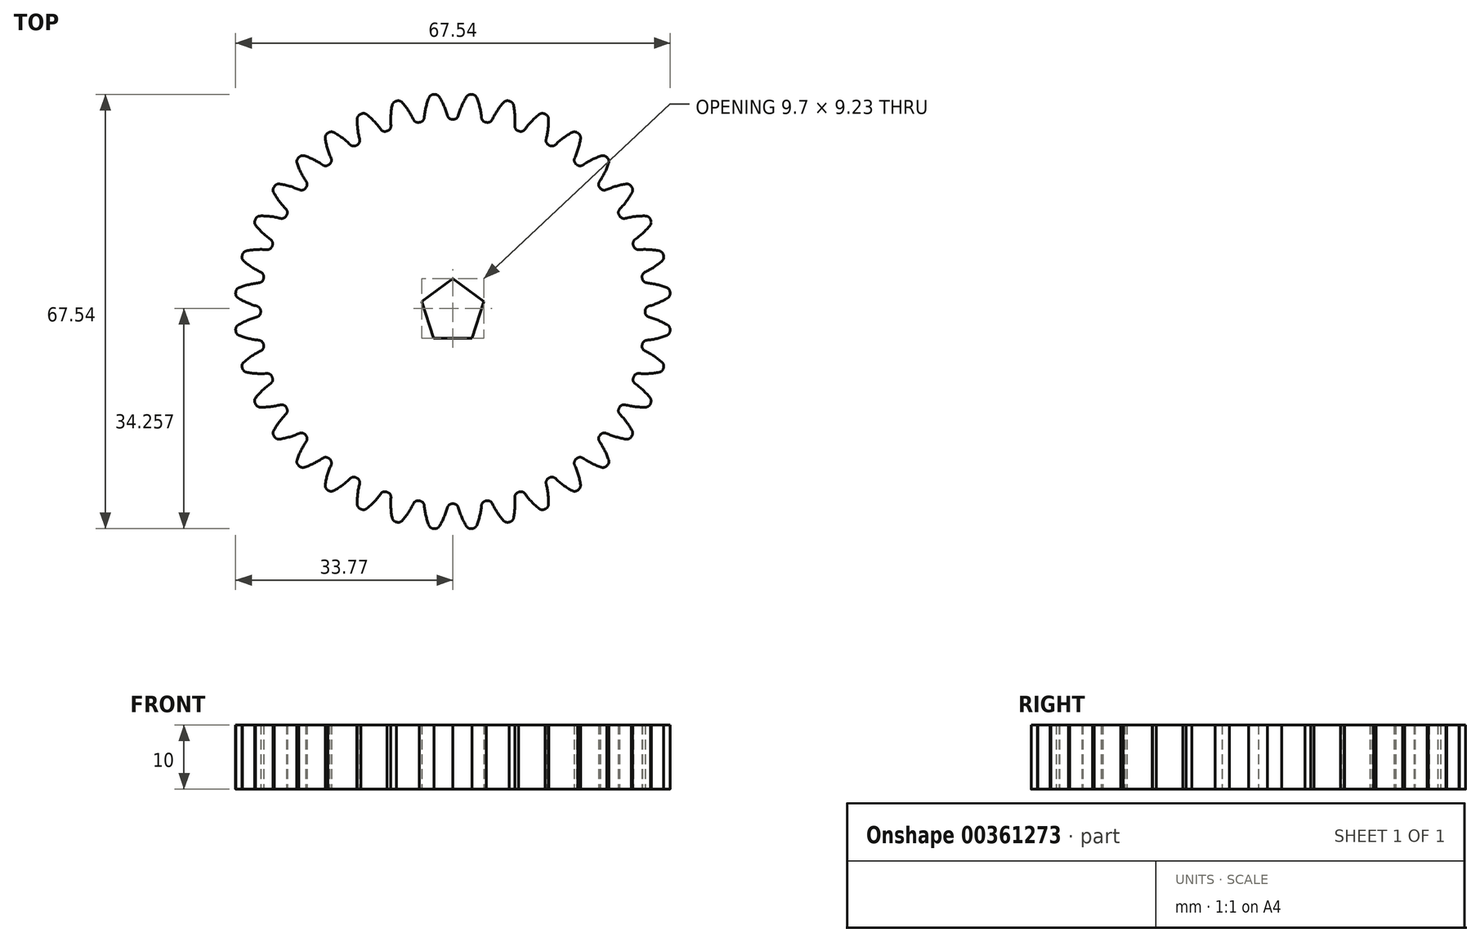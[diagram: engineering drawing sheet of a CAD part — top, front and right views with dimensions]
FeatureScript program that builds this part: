
annotation { "Feature Type Name" : "Feature", "Feature Type Description" : "" }
export const myFeature = defineFeature(function(context is Context, id is Id, definition is map)
    precondition{}
    {
        {
            var Q0;
            Q0=qCreatedBy(makeId("Top.planeOp"),FACE);
            var sketch = newSketch(context, id + "F0", { "sketchPlane" : qUnion([Q0])});
            skCircle(sketch, "E0", {"center": v(0, 0) * mm, "radius": 32.1 * mm, "construction": true});
            skCircle(sketch, "E1", {"center": v(0, 0) * mm, "radius": 33.88 * mm, "construction": true});
            skCircle(sketch, "E2", {"center": v(0, 0) * mm, "radius": 29.88 * mm, "construction": true});
            skLineSegment(sketch, "E3", {"start": v(0, 0) * mm, "end": v(0, 35.03) * mm, "construction": true});
            skLineSegment(sketch, "E4", {"start": v(0, 0) * mm, "end": v(-6.12, 34.73) * mm, "construction": true});
            skLineSegment(sketch, "E5", {"start": v(0, 0) * mm, "end": v(-3.06, 35) * mm, "construction": true});
            skCircle(sketch, "E6", {"center": v(-2.8, 31.98) * mm, "radius": 1.4 * mm, "construction": true});
            skCircle(sketch, "E7", {"center": v(-2.8, 31.98) * mm, "radius": 10 * mm, "construction": true});
            skArc(sketch, "E8", {"start": v(-1.92, 21.9) * mm, "mid": v(-1.88, 21.97) * mm, "end": v(-1.85, 22.02) * mm});
            skArc(sketch, "E9.trimOffspring", {"start": v(-0.85, 30.47) * mm, "mid": v(-1.38, 31.97) * mm, "end": v(-2.11, 33.38) * mm});
            skLineSegment(sketch, "E10", {"start": v(-2.85, 33.76) * mm, "end": v(-2.95, 33.76) * mm});
            skLineSegment(sketch, "E11", {"start": v(-0.07, 29.88) * mm, "end": v(0, 29.88) * mm});
            skPoint(sketch, "E12.visualSharp", {"position": v(-0.7, 29.87) * mm});
            skArc(sketch, "E12.filletArc", {"start": v(-0.85, 30.47) * mm, "mid": v(-0.56, 30.04) * mm, "end": v(-0.07, 29.88) * mm});
            skPoint(sketch, "E13.visualSharp", {"position": v(-2.38, 33.8) * mm});
            skArc(sketch, "E13.filletArc", {"start": v(-2.11, 33.38) * mm, "mid": v(-2.43, 33.68) * mm, "end": v(-2.85, 33.76) * mm});
            skArc(sketch, "E14.MirrorCS", {"start": v(-4.46, 30.15) * mm, "mid": v(-4.67, 29.68) * mm, "end": v(-5.12, 29.44) * mm});
            skLineSegment(sketch, "E15.MirrorCS", {"start": v(-5.12, 29.44) * mm, "end": v(-5.19, 29.43) * mm});
            skArc(sketch, "E16.MirrorCS", {"start": v(-4.46, 30.15) * mm, "mid": v(-4.2, 31.72) * mm, "end": v(-3.72, 33.24) * mm});
            skArc(sketch, "E17.MirrorCS", {"start": v(-3.72, 33.24) * mm, "mid": v(-3.46, 33.59) * mm, "end": v(-3.06, 33.75) * mm});
            skLineSegment(sketch, "E18.MirrorCS", {"start": v(-3.06, 33.75) * mm, "end": v(-2.95, 33.76) * mm});
            skArc(sketch, "E19.1.0", {"start": v(-6.12, 29.86) * mm, "mid": v(-5.76, 29.49) * mm, "end": v(-5.25, 29.41) * mm});
            skLineSegment(sketch, "E19.1.1", {"start": v(-5.25, 29.41) * mm, "end": v(-5.19, 29.43) * mm});
            skArc(sketch, "E19.1.2", {"start": v(-6.12, 29.86) * mm, "mid": v(-6.9, 31.25) * mm, "end": v(-7.88, 32.51) * mm});
            skArc(sketch, "E19.1.3", {"start": v(-7.88, 32.51) * mm, "mid": v(-8.24, 32.74) * mm, "end": v(-8.67, 32.76) * mm});
            skLineSegment(sketch, "E19.1.4", {"start": v(-8.67, 32.76) * mm, "end": v(-8.77, 32.73) * mm});
            skLineSegment(sketch, "E19.1.5", {"start": v(-8.87, 32.7) * mm, "end": v(-8.77, 32.73) * mm});
            skArc(sketch, "E19.1.6", {"start": v(-9.43, 32.1) * mm, "mid": v(-9.24, 32.48) * mm, "end": v(-8.87, 32.7) * mm});
            skArc(sketch, "E19.1.7", {"start": v(-9.63, 28.92) * mm, "mid": v(-9.64, 30.51) * mm, "end": v(-9.43, 32.1) * mm});
            skArc(sketch, "E19.1.8", {"start": v(-9.63, 28.92) * mm, "mid": v(-9.75, 28.42) * mm, "end": v(-10.16, 28.1) * mm});
            skLineSegment(sketch, "E19.1.9", {"start": v(-10.16, 28.1) * mm, "end": v(-10.22, 28.08) * mm});
            skArc(sketch, "E19.2.0", {"start": v(-11.22, 28.34) * mm, "mid": v(-10.8, 28.04) * mm, "end": v(-10.28, 28.05) * mm});
            skLineSegment(sketch, "E19.2.1", {"start": v(-10.28, 28.05) * mm, "end": v(-10.22, 28.08) * mm});
            skArc(sketch, "E19.2.2", {"start": v(-11.22, 28.34) * mm, "mid": v(-12.23, 29.57) * mm, "end": v(-13.4, 30.65) * mm});
            skArc(sketch, "E19.2.3", {"start": v(-13.4, 30.65) * mm, "mid": v(-13.8, 30.82) * mm, "end": v(-14.22, 30.75) * mm});
            skLineSegment(sketch, "E19.2.4", {"start": v(-14.22, 30.75) * mm, "end": v(-14.32, 30.71) * mm});
            skLineSegment(sketch, "E19.2.5", {"start": v(-14.41, 30.66) * mm, "end": v(-14.32, 30.71) * mm});
            skArc(sketch, "E19.2.6", {"start": v(-14.86, 29.97) * mm, "mid": v(-14.74, 30.38) * mm, "end": v(-14.41, 30.66) * mm});
            skArc(sketch, "E19.2.7", {"start": v(-14.5, 26.8) * mm, "mid": v(-14.8, 28.37) * mm, "end": v(-14.86, 29.97) * mm});
            skArc(sketch, "E19.2.8", {"start": v(-14.5, 26.8) * mm, "mid": v(-14.54, 26.3) * mm, "end": v(-14.88, 25.9) * mm});
            skLineSegment(sketch, "E19.2.9", {"start": v(-14.88, 25.9) * mm, "end": v(-14.94, 25.88) * mm});
            skArc(sketch, "E19.3.0", {"start": v(-15.97, 25.96) * mm, "mid": v(-15.5, 25.74) * mm, "end": v(-15, 25.84) * mm});
            skLineSegment(sketch, "E19.3.1", {"start": v(-15, 25.84) * mm, "end": v(-14.94, 25.88) * mm});
            skArc(sketch, "E19.3.2", {"start": v(-15.97, 25.96) * mm, "mid": v(-17.18, 27) * mm, "end": v(-18.52, 27.86) * mm});
            skArc(sketch, "E19.3.3", {"start": v(-18.52, 27.86) * mm, "mid": v(-18.94, 27.95) * mm, "end": v(-19.35, 27.82) * mm});
            skLineSegment(sketch, "E19.3.4", {"start": v(-19.35, 27.82) * mm, "end": v(-19.44, 27.76) * mm});
            skLineSegment(sketch, "E19.3.5", {"start": v(-19.52, 27.7) * mm, "end": v(-19.44, 27.76) * mm});
            skArc(sketch, "E19.3.6", {"start": v(-19.84, 26.93) * mm, "mid": v(-19.79, 27.36) * mm, "end": v(-19.52, 27.7) * mm});
            skArc(sketch, "E19.3.7", {"start": v(-18.94, 23.88) * mm, "mid": v(-19.5, 25.37) * mm, "end": v(-19.84, 26.93) * mm});
            skArc(sketch, "E19.3.8", {"start": v(-18.94, 23.88) * mm, "mid": v(-18.88, 23.37) * mm, "end": v(-19.16, 22.93) * mm});
            skLineSegment(sketch, "E19.3.9", {"start": v(-19.16, 22.93) * mm, "end": v(-19.2, 22.89) * mm});
            skArc(sketch, "E19.4.0", {"start": v(-20.23, 22.8) * mm, "mid": v(-19.74, 22.65) * mm, "end": v(-19.26, 22.85) * mm});
            skLineSegment(sketch, "E19.4.1", {"start": v(-19.26, 22.85) * mm, "end": v(-19.2, 22.89) * mm});
            skArc(sketch, "E19.4.2", {"start": v(-20.23, 22.8) * mm, "mid": v(-21.6, 23.6) * mm, "end": v(-23.08, 24.22) * mm});
            skArc(sketch, "E19.4.3", {"start": v(-23.08, 24.22) * mm, "mid": v(-23.5, 24.24) * mm, "end": v(-23.88, 24.03) * mm});
            skLineSegment(sketch, "E19.4.4", {"start": v(-23.88, 24.03) * mm, "end": v(-23.96, 23.96) * mm});
            skLineSegment(sketch, "E19.4.5", {"start": v(-24.03, 23.88) * mm, "end": v(-23.96, 23.96) * mm});
            skArc(sketch, "E19.4.6", {"start": v(-24.22, 23.08) * mm, "mid": v(-24.24, 23.5) * mm, "end": v(-24.03, 23.88) * mm});
            skArc(sketch, "E19.4.7", {"start": v(-22.8, 20.23) * mm, "mid": v(-23.6, 21.6) * mm, "end": v(-24.22, 23.08) * mm});
            skArc(sketch, "E19.4.8", {"start": v(-22.8, 20.23) * mm, "mid": v(-22.65, 19.74) * mm, "end": v(-22.85, 19.26) * mm});
            skLineSegment(sketch, "E19.4.9", {"start": v(-22.85, 19.26) * mm, "end": v(-22.89, 19.2) * mm});
            skArc(sketch, "E19.5.0", {"start": v(-23.88, 18.94) * mm, "mid": v(-23.37, 18.88) * mm, "end": v(-22.93, 19.16) * mm});
            skLineSegment(sketch, "E19.5.1", {"start": v(-22.93, 19.16) * mm, "end": v(-22.89, 19.2) * mm});
            skArc(sketch, "E19.5.2", {"start": v(-23.88, 18.94) * mm, "mid": v(-25.37, 19.5) * mm, "end": v(-26.93, 19.84) * mm});
            skArc(sketch, "E19.5.3", {"start": v(-26.93, 19.84) * mm, "mid": v(-27.36, 19.79) * mm, "end": v(-27.7, 19.52) * mm});
            skLineSegment(sketch, "E19.5.4", {"start": v(-27.7, 19.52) * mm, "end": v(-27.76, 19.44) * mm});
            skLineSegment(sketch, "E19.5.5", {"start": v(-27.82, 19.35) * mm, "end": v(-27.76, 19.44) * mm});
            skArc(sketch, "E19.5.6", {"start": v(-27.86, 18.52) * mm, "mid": v(-27.95, 18.94) * mm, "end": v(-27.82, 19.35) * mm});
            skArc(sketch, "E19.5.7", {"start": v(-25.96, 15.97) * mm, "mid": v(-27, 17.18) * mm, "end": v(-27.86, 18.52) * mm});
            skArc(sketch, "E19.5.8", {"start": v(-25.96, 15.97) * mm, "mid": v(-25.74, 15.5) * mm, "end": v(-25.84, 15) * mm});
            skLineSegment(sketch, "E19.5.9", {"start": v(-25.84, 15) * mm, "end": v(-25.88, 14.94) * mm});
            skArc(sketch, "E19.6.0", {"start": v(-26.8, 14.5) * mm, "mid": v(-26.3, 14.54) * mm, "end": v(-25.9, 14.88) * mm});
            skLineSegment(sketch, "E19.6.1", {"start": v(-25.9, 14.88) * mm, "end": v(-25.88, 14.94) * mm});
            skArc(sketch, "E19.6.2", {"start": v(-26.8, 14.5) * mm, "mid": v(-28.37, 14.8) * mm, "end": v(-29.97, 14.86) * mm});
            skArc(sketch, "E19.6.3", {"start": v(-29.97, 14.86) * mm, "mid": v(-30.38, 14.74) * mm, "end": v(-30.66, 14.41) * mm});
            skLineSegment(sketch, "E19.6.4", {"start": v(-30.66, 14.41) * mm, "end": v(-30.71, 14.32) * mm});
            skLineSegment(sketch, "E19.6.5", {"start": v(-30.75, 14.22) * mm, "end": v(-30.71, 14.32) * mm});
            skArc(sketch, "E19.6.6", {"start": v(-30.65, 13.4) * mm, "mid": v(-30.82, 13.8) * mm, "end": v(-30.75, 14.22) * mm});
            skArc(sketch, "E19.6.7", {"start": v(-28.34, 11.22) * mm, "mid": v(-29.57, 12.23) * mm, "end": v(-30.65, 13.4) * mm});
            skArc(sketch, "E19.6.8", {"start": v(-28.34, 11.22) * mm, "mid": v(-28.04, 10.8) * mm, "end": v(-28.05, 10.28) * mm});
            skLineSegment(sketch, "E19.6.9", {"start": v(-28.05, 10.28) * mm, "end": v(-28.08, 10.22) * mm});
            skArc(sketch, "E19.7.0", {"start": v(-28.92, 9.63) * mm, "mid": v(-28.42, 9.75) * mm, "end": v(-28.1, 10.16) * mm});
            skLineSegment(sketch, "E19.7.1", {"start": v(-28.1, 10.16) * mm, "end": v(-28.08, 10.22) * mm});
            skArc(sketch, "E19.7.2", {"start": v(-28.92, 9.63) * mm, "mid": v(-30.51, 9.64) * mm, "end": v(-32.1, 9.43) * mm});
            skArc(sketch, "E19.7.3", {"start": v(-32.1, 9.43) * mm, "mid": v(-32.48, 9.24) * mm, "end": v(-32.7, 8.87) * mm});
            skLineSegment(sketch, "E19.7.4", {"start": v(-32.7, 8.87) * mm, "end": v(-32.73, 8.77) * mm});
            skLineSegment(sketch, "E19.7.5", {"start": v(-32.76, 8.67) * mm, "end": v(-32.73, 8.77) * mm});
            skArc(sketch, "E19.7.6", {"start": v(-32.51, 7.88) * mm, "mid": v(-32.74, 8.24) * mm, "end": v(-32.76, 8.67) * mm});
            skArc(sketch, "E19.7.7", {"start": v(-29.86, 6.12) * mm, "mid": v(-31.25, 6.9) * mm, "end": v(-32.51, 7.88) * mm});
            skArc(sketch, "E19.7.8", {"start": v(-29.86, 6.12) * mm, "mid": v(-29.49, 5.76) * mm, "end": v(-29.41, 5.25) * mm});
            skLineSegment(sketch, "E19.7.9", {"start": v(-29.41, 5.25) * mm, "end": v(-29.43, 5.19) * mm});
            skArc(sketch, "E19.8.0", {"start": v(-30.15, 4.46) * mm, "mid": v(-29.68, 4.67) * mm, "end": v(-29.44, 5.12) * mm});
            skLineSegment(sketch, "E19.8.1", {"start": v(-29.44, 5.12) * mm, "end": v(-29.43, 5.19) * mm});
            skArc(sketch, "E19.8.2", {"start": v(-30.15, 4.46) * mm, "mid": v(-31.72, 4.2) * mm, "end": v(-33.24, 3.72) * mm});
            skArc(sketch, "E19.8.3", {"start": v(-33.24, 3.72) * mm, "mid": v(-33.59, 3.46) * mm, "end": v(-33.75, 3.06) * mm});
            skLineSegment(sketch, "E19.8.4", {"start": v(-33.75, 3.06) * mm, "end": v(-33.76, 2.95) * mm});
            skLineSegment(sketch, "E19.8.5", {"start": v(-33.76, 2.85) * mm, "end": v(-33.76, 2.95) * mm});
            skArc(sketch, "E19.8.6", {"start": v(-33.38, 2.11) * mm, "mid": v(-33.68, 2.43) * mm, "end": v(-33.76, 2.85) * mm});
            skArc(sketch, "E19.8.7", {"start": v(-30.47, 0.85) * mm, "mid": v(-31.97, 1.38) * mm, "end": v(-33.38, 2.11) * mm});
            skArc(sketch, "E19.8.8", {"start": v(-30.47, 0.85) * mm, "mid": v(-30.04, 0.56) * mm, "end": v(-29.88, 0.07) * mm});
            skLineSegment(sketch, "E19.8.9", {"start": v(-29.88, 0.07) * mm, "end": v(-29.88, 0) * mm});
            skArc(sketch, "E19.9.0", {"start": v(-30.47, -0.85) * mm, "mid": v(-30.04, -0.56) * mm, "end": v(-29.88, -0.07) * mm});
            skLineSegment(sketch, "E19.9.1", {"start": v(-29.88, -0.07) * mm, "end": v(-29.88, 0) * mm});
            skArc(sketch, "E19.9.2", {"start": v(-30.47, -0.85) * mm, "mid": v(-31.97, -1.38) * mm, "end": v(-33.38, -2.11) * mm});
            skArc(sketch, "E19.9.3", {"start": v(-33.38, -2.11) * mm, "mid": v(-33.68, -2.43) * mm, "end": v(-33.76, -2.85) * mm});
            skLineSegment(sketch, "E19.9.4", {"start": v(-33.76, -2.85) * mm, "end": v(-33.76, -2.95) * mm});
            skLineSegment(sketch, "E19.9.5", {"start": v(-33.75, -3.06) * mm, "end": v(-33.76, -2.95) * mm});
            skArc(sketch, "E19.9.6", {"start": v(-33.24, -3.72) * mm, "mid": v(-33.59, -3.46) * mm, "end": v(-33.75, -3.06) * mm});
            skArc(sketch, "E19.9.7", {"start": v(-30.15, -4.46) * mm, "mid": v(-31.72, -4.2) * mm, "end": v(-33.24, -3.72) * mm});
            skArc(sketch, "E19.9.8", {"start": v(-30.15, -4.46) * mm, "mid": v(-29.68, -4.67) * mm, "end": v(-29.44, -5.12) * mm});
            skLineSegment(sketch, "E19.9.9", {"start": v(-29.44, -5.12) * mm, "end": v(-29.43, -5.19) * mm});
            skArc(sketch, "E19.10.0", {"start": v(-29.86, -6.12) * mm, "mid": v(-29.49, -5.76) * mm, "end": v(-29.41, -5.25) * mm});
            skLineSegment(sketch, "E19.10.1", {"start": v(-29.41, -5.25) * mm, "end": v(-29.43, -5.19) * mm});
            skArc(sketch, "E19.10.2", {"start": v(-29.86, -6.12) * mm, "mid": v(-31.25, -6.9) * mm, "end": v(-32.51, -7.88) * mm});
            skArc(sketch, "E19.10.3", {"start": v(-32.51, -7.88) * mm, "mid": v(-32.74, -8.24) * mm, "end": v(-32.76, -8.67) * mm});
            skLineSegment(sketch, "E19.10.4", {"start": v(-32.76, -8.67) * mm, "end": v(-32.73, -8.77) * mm});
            skLineSegment(sketch, "E19.10.5", {"start": v(-32.7, -8.87) * mm, "end": v(-32.73, -8.77) * mm});
            skArc(sketch, "E19.10.6", {"start": v(-32.1, -9.43) * mm, "mid": v(-32.48, -9.24) * mm, "end": v(-32.7, -8.87) * mm});
            skArc(sketch, "E19.10.7", {"start": v(-28.92, -9.63) * mm, "mid": v(-30.51, -9.64) * mm, "end": v(-32.1, -9.43) * mm});
            skArc(sketch, "E19.10.8", {"start": v(-28.92, -9.63) * mm, "mid": v(-28.42, -9.75) * mm, "end": v(-28.1, -10.16) * mm});
            skLineSegment(sketch, "E19.10.9", {"start": v(-28.1, -10.16) * mm, "end": v(-28.08, -10.22) * mm});
            skArc(sketch, "E19.11.0", {"start": v(-28.34, -11.22) * mm, "mid": v(-28.04, -10.8) * mm, "end": v(-28.05, -10.28) * mm});
            skLineSegment(sketch, "E19.11.1", {"start": v(-28.05, -10.28) * mm, "end": v(-28.08, -10.22) * mm});
            skArc(sketch, "E19.11.2", {"start": v(-28.34, -11.22) * mm, "mid": v(-29.57, -12.23) * mm, "end": v(-30.65, -13.4) * mm});
            skArc(sketch, "E19.11.3", {"start": v(-30.65, -13.4) * mm, "mid": v(-30.82, -13.8) * mm, "end": v(-30.75, -14.22) * mm});
            skLineSegment(sketch, "E19.11.4", {"start": v(-30.75, -14.22) * mm, "end": v(-30.71, -14.32) * mm});
            skLineSegment(sketch, "E19.11.5", {"start": v(-30.66, -14.41) * mm, "end": v(-30.71, -14.32) * mm});
            skArc(sketch, "E19.11.6", {"start": v(-29.97, -14.86) * mm, "mid": v(-30.38, -14.74) * mm, "end": v(-30.66, -14.41) * mm});
            skArc(sketch, "E19.11.7", {"start": v(-26.8, -14.5) * mm, "mid": v(-28.37, -14.8) * mm, "end": v(-29.97, -14.86) * mm});
            skArc(sketch, "E19.11.8", {"start": v(-26.8, -14.5) * mm, "mid": v(-26.3, -14.54) * mm, "end": v(-25.9, -14.88) * mm});
            skLineSegment(sketch, "E19.11.9", {"start": v(-25.9, -14.88) * mm, "end": v(-25.88, -14.94) * mm});
            skArc(sketch, "E19.12.0", {"start": v(-25.96, -15.97) * mm, "mid": v(-25.74, -15.5) * mm, "end": v(-25.84, -15) * mm});
            skLineSegment(sketch, "E19.12.1", {"start": v(-25.84, -15) * mm, "end": v(-25.88, -14.94) * mm});
            skArc(sketch, "E19.12.2", {"start": v(-25.96, -15.97) * mm, "mid": v(-27, -17.18) * mm, "end": v(-27.86, -18.52) * mm});
            skArc(sketch, "E19.12.3", {"start": v(-27.86, -18.52) * mm, "mid": v(-27.95, -18.94) * mm, "end": v(-27.82, -19.35) * mm});
            skLineSegment(sketch, "E19.12.4", {"start": v(-27.82, -19.35) * mm, "end": v(-27.76, -19.44) * mm});
            skLineSegment(sketch, "E19.12.5", {"start": v(-27.7, -19.52) * mm, "end": v(-27.76, -19.44) * mm});
            skArc(sketch, "E19.12.6", {"start": v(-26.93, -19.84) * mm, "mid": v(-27.36, -19.79) * mm, "end": v(-27.7, -19.52) * mm});
            skArc(sketch, "E19.12.7", {"start": v(-23.88, -18.94) * mm, "mid": v(-25.37, -19.5) * mm, "end": v(-26.93, -19.84) * mm});
            skArc(sketch, "E19.12.8", {"start": v(-23.88, -18.94) * mm, "mid": v(-23.37, -18.88) * mm, "end": v(-22.93, -19.16) * mm});
            skLineSegment(sketch, "E19.12.9", {"start": v(-22.93, -19.16) * mm, "end": v(-22.89, -19.2) * mm});
            skArc(sketch, "E19.13.0", {"start": v(-22.8, -20.23) * mm, "mid": v(-22.65, -19.74) * mm, "end": v(-22.85, -19.26) * mm});
            skLineSegment(sketch, "E19.13.1", {"start": v(-22.85, -19.26) * mm, "end": v(-22.89, -19.2) * mm});
            skArc(sketch, "E19.13.2", {"start": v(-22.8, -20.23) * mm, "mid": v(-23.6, -21.6) * mm, "end": v(-24.22, -23.08) * mm});
            skArc(sketch, "E19.13.3", {"start": v(-24.22, -23.08) * mm, "mid": v(-24.24, -23.5) * mm, "end": v(-24.03, -23.88) * mm});
            skLineSegment(sketch, "E19.13.4", {"start": v(-24.03, -23.88) * mm, "end": v(-23.96, -23.96) * mm});
            skLineSegment(sketch, "E19.13.5", {"start": v(-23.88, -24.03) * mm, "end": v(-23.96, -23.96) * mm});
            skArc(sketch, "E19.13.6", {"start": v(-23.08, -24.22) * mm, "mid": v(-23.5, -24.24) * mm, "end": v(-23.88, -24.03) * mm});
            skArc(sketch, "E19.13.7", {"start": v(-20.23, -22.8) * mm, "mid": v(-21.6, -23.6) * mm, "end": v(-23.08, -24.22) * mm});
            skArc(sketch, "E19.13.8", {"start": v(-20.23, -22.8) * mm, "mid": v(-19.74, -22.65) * mm, "end": v(-19.26, -22.85) * mm});
            skLineSegment(sketch, "E19.13.9", {"start": v(-19.26, -22.85) * mm, "end": v(-19.2, -22.89) * mm});
            skArc(sketch, "E19.14.0", {"start": v(-18.94, -23.88) * mm, "mid": v(-18.88, -23.37) * mm, "end": v(-19.16, -22.93) * mm});
            skLineSegment(sketch, "E19.14.1", {"start": v(-19.16, -22.93) * mm, "end": v(-19.2, -22.89) * mm});
            skArc(sketch, "E19.14.2", {"start": v(-18.94, -23.88) * mm, "mid": v(-19.5, -25.37) * mm, "end": v(-19.84, -26.93) * mm});
            skArc(sketch, "E19.14.3", {"start": v(-19.84, -26.93) * mm, "mid": v(-19.79, -27.36) * mm, "end": v(-19.52, -27.7) * mm});
            skLineSegment(sketch, "E19.14.4", {"start": v(-19.52, -27.7) * mm, "end": v(-19.44, -27.76) * mm});
            skLineSegment(sketch, "E19.14.5", {"start": v(-19.35, -27.82) * mm, "end": v(-19.44, -27.76) * mm});
            skArc(sketch, "E19.14.6", {"start": v(-18.52, -27.86) * mm, "mid": v(-18.94, -27.95) * mm, "end": v(-19.35, -27.82) * mm});
            skArc(sketch, "E19.14.7", {"start": v(-15.97, -25.96) * mm, "mid": v(-17.18, -27) * mm, "end": v(-18.52, -27.86) * mm});
            skArc(sketch, "E19.14.8", {"start": v(-15.97, -25.96) * mm, "mid": v(-15.5, -25.74) * mm, "end": v(-15, -25.84) * mm});
            skLineSegment(sketch, "E19.14.9", {"start": v(-15, -25.84) * mm, "end": v(-14.94, -25.88) * mm});
            skArc(sketch, "E19.15.0", {"start": v(-14.5, -26.8) * mm, "mid": v(-14.54, -26.3) * mm, "end": v(-14.88, -25.9) * mm});
            skLineSegment(sketch, "E19.15.1", {"start": v(-14.88, -25.9) * mm, "end": v(-14.94, -25.88) * mm});
            skArc(sketch, "E19.15.2", {"start": v(-14.5, -26.8) * mm, "mid": v(-14.8, -28.37) * mm, "end": v(-14.86, -29.97) * mm});
            skArc(sketch, "E19.15.3", {"start": v(-14.86, -29.97) * mm, "mid": v(-14.74, -30.38) * mm, "end": v(-14.41, -30.66) * mm});
            skLineSegment(sketch, "E19.15.4", {"start": v(-14.41, -30.66) * mm, "end": v(-14.32, -30.71) * mm});
            skLineSegment(sketch, "E19.15.5", {"start": v(-14.22, -30.75) * mm, "end": v(-14.32, -30.71) * mm});
            skArc(sketch, "E19.15.6", {"start": v(-13.4, -30.65) * mm, "mid": v(-13.8, -30.82) * mm, "end": v(-14.22, -30.75) * mm});
            skArc(sketch, "E19.15.7", {"start": v(-11.22, -28.34) * mm, "mid": v(-12.23, -29.57) * mm, "end": v(-13.4, -30.65) * mm});
            skArc(sketch, "E19.15.8", {"start": v(-11.22, -28.34) * mm, "mid": v(-10.8, -28.04) * mm, "end": v(-10.28, -28.05) * mm});
            skLineSegment(sketch, "E19.15.9", {"start": v(-10.28, -28.05) * mm, "end": v(-10.22, -28.08) * mm});
            skArc(sketch, "E19.16.0", {"start": v(-9.63, -28.92) * mm, "mid": v(-9.75, -28.42) * mm, "end": v(-10.16, -28.1) * mm});
            skLineSegment(sketch, "E19.16.1", {"start": v(-10.16, -28.1) * mm, "end": v(-10.22, -28.08) * mm});
            skArc(sketch, "E19.16.2", {"start": v(-9.63, -28.92) * mm, "mid": v(-9.64, -30.51) * mm, "end": v(-9.43, -32.1) * mm});
            skArc(sketch, "E19.16.3", {"start": v(-9.43, -32.1) * mm, "mid": v(-9.24, -32.48) * mm, "end": v(-8.87, -32.7) * mm});
            skLineSegment(sketch, "E19.16.4", {"start": v(-8.87, -32.7) * mm, "end": v(-8.77, -32.73) * mm});
            skLineSegment(sketch, "E19.16.5", {"start": v(-8.67, -32.76) * mm, "end": v(-8.77, -32.73) * mm});
            skArc(sketch, "E19.16.6", {"start": v(-7.88, -32.5) * mm, "mid": v(-8.24, -32.74) * mm, "end": v(-8.67, -32.76) * mm});
            skArc(sketch, "E19.16.7", {"start": v(-6.12, -29.86) * mm, "mid": v(-6.9, -31.25) * mm, "end": v(-7.88, -32.5) * mm});
            skArc(sketch, "E19.16.8", {"start": v(-6.12, -29.86) * mm, "mid": v(-5.76, -29.49) * mm, "end": v(-5.25, -29.41) * mm});
            skLineSegment(sketch, "E19.16.9", {"start": v(-5.25, -29.41) * mm, "end": v(-5.19, -29.43) * mm});
            skArc(sketch, "E19.17.0", {"start": v(-4.46, -30.15) * mm, "mid": v(-4.67, -29.68) * mm, "end": v(-5.12, -29.44) * mm});
            skLineSegment(sketch, "E19.17.1", {"start": v(-5.12, -29.44) * mm, "end": v(-5.19, -29.43) * mm});
            skArc(sketch, "E19.17.2", {"start": v(-4.46, -30.15) * mm, "mid": v(-4.2, -31.72) * mm, "end": v(-3.72, -33.24) * mm});
            skArc(sketch, "E19.17.3", {"start": v(-3.72, -33.24) * mm, "mid": v(-3.46, -33.59) * mm, "end": v(-3.06, -33.74) * mm});
            skLineSegment(sketch, "E19.17.4", {"start": v(-3.06, -33.74) * mm, "end": v(-2.95, -33.76) * mm});
            skLineSegment(sketch, "E19.17.5", {"start": v(-2.85, -33.76) * mm, "end": v(-2.95, -33.76) * mm});
            skArc(sketch, "E19.17.6", {"start": v(-2.11, -33.38) * mm, "mid": v(-2.43, -33.68) * mm, "end": v(-2.85, -33.76) * mm});
            skArc(sketch, "E19.17.7", {"start": v(-0.85, -30.47) * mm, "mid": v(-1.38, -31.97) * mm, "end": v(-2.11, -33.38) * mm});
            skArc(sketch, "E19.17.8", {"start": v(-0.85, -30.47) * mm, "mid": v(-0.56, -30.04) * mm, "end": v(-0.07, -29.88) * mm});
            skLineSegment(sketch, "E19.17.9", {"start": v(-0.07, -29.88) * mm, "end": v(0, -29.88) * mm});
            skArc(sketch, "E19.18.0", {"start": v(0.85, -30.47) * mm, "mid": v(0.56, -30.04) * mm, "end": v(0.07, -29.88) * mm});
            skLineSegment(sketch, "E19.18.1", {"start": v(0.07, -29.88) * mm, "end": v(0, -29.88) * mm});
            skArc(sketch, "E19.18.2", {"start": v(0.85, -30.47) * mm, "mid": v(1.38, -31.97) * mm, "end": v(2.11, -33.38) * mm});
            skArc(sketch, "E19.18.3", {"start": v(2.11, -33.38) * mm, "mid": v(2.43, -33.68) * mm, "end": v(2.85, -33.76) * mm});
            skLineSegment(sketch, "E19.18.4", {"start": v(2.85, -33.76) * mm, "end": v(2.95, -33.76) * mm});
            skLineSegment(sketch, "E19.18.5", {"start": v(3.06, -33.74) * mm, "end": v(2.95, -33.76) * mm});
            skArc(sketch, "E19.18.6", {"start": v(3.72, -33.24) * mm, "mid": v(3.46, -33.59) * mm, "end": v(3.06, -33.74) * mm});
            skArc(sketch, "E19.18.7", {"start": v(4.46, -30.15) * mm, "mid": v(4.2, -31.72) * mm, "end": v(3.72, -33.24) * mm});
            skArc(sketch, "E19.18.8", {"start": v(4.46, -30.15) * mm, "mid": v(4.67, -29.68) * mm, "end": v(5.12, -29.44) * mm});
            skLineSegment(sketch, "E19.18.9", {"start": v(5.12, -29.44) * mm, "end": v(5.19, -29.43) * mm});
            skArc(sketch, "E19.19.0", {"start": v(6.12, -29.86) * mm, "mid": v(5.76, -29.49) * mm, "end": v(5.25, -29.41) * mm});
            skLineSegment(sketch, "E19.19.1", {"start": v(5.25, -29.41) * mm, "end": v(5.19, -29.43) * mm});
            skArc(sketch, "E19.19.2", {"start": v(6.12, -29.86) * mm, "mid": v(6.9, -31.25) * mm, "end": v(7.88, -32.5) * mm});
            skArc(sketch, "E19.19.3", {"start": v(7.88, -32.5) * mm, "mid": v(8.24, -32.74) * mm, "end": v(8.67, -32.76) * mm});
            skLineSegment(sketch, "E19.19.4", {"start": v(8.67, -32.76) * mm, "end": v(8.77, -32.73) * mm});
            skLineSegment(sketch, "E19.19.5", {"start": v(8.87, -32.7) * mm, "end": v(8.77, -32.73) * mm});
            skArc(sketch, "E19.19.6", {"start": v(9.43, -32.1) * mm, "mid": v(9.24, -32.48) * mm, "end": v(8.87, -32.7) * mm});
            skArc(sketch, "E19.19.7", {"start": v(9.63, -28.92) * mm, "mid": v(9.64, -30.51) * mm, "end": v(9.43, -32.1) * mm});
            skArc(sketch, "E19.19.8", {"start": v(9.63, -28.92) * mm, "mid": v(9.75, -28.42) * mm, "end": v(10.16, -28.1) * mm});
            skLineSegment(sketch, "E19.19.9", {"start": v(10.16, -28.1) * mm, "end": v(10.22, -28.08) * mm});
            skArc(sketch, "E19.20.0", {"start": v(11.22, -28.34) * mm, "mid": v(10.8, -28.04) * mm, "end": v(10.28, -28.05) * mm});
            skLineSegment(sketch, "E19.20.1", {"start": v(10.28, -28.05) * mm, "end": v(10.22, -28.08) * mm});
            skArc(sketch, "E19.20.2", {"start": v(11.22, -28.34) * mm, "mid": v(12.23, -29.57) * mm, "end": v(13.4, -30.65) * mm});
            skArc(sketch, "E19.20.3", {"start": v(13.4, -30.65) * mm, "mid": v(13.8, -30.82) * mm, "end": v(14.22, -30.75) * mm});
            skLineSegment(sketch, "E19.20.4", {"start": v(14.22, -30.75) * mm, "end": v(14.32, -30.71) * mm});
            skLineSegment(sketch, "E19.20.5", {"start": v(14.41, -30.66) * mm, "end": v(14.32, -30.71) * mm});
            skArc(sketch, "E19.20.6", {"start": v(14.86, -29.97) * mm, "mid": v(14.74, -30.38) * mm, "end": v(14.41, -30.66) * mm});
            skArc(sketch, "E19.20.7", {"start": v(14.5, -26.8) * mm, "mid": v(14.8, -28.37) * mm, "end": v(14.86, -29.97) * mm});
            skArc(sketch, "E19.20.8", {"start": v(14.5, -26.8) * mm, "mid": v(14.54, -26.3) * mm, "end": v(14.88, -25.9) * mm});
            skLineSegment(sketch, "E19.20.9", {"start": v(14.88, -25.9) * mm, "end": v(14.94, -25.88) * mm});
            skArc(sketch, "E19.21.0", {"start": v(15.97, -25.96) * mm, "mid": v(15.5, -25.74) * mm, "end": v(15, -25.84) * mm});
            skLineSegment(sketch, "E19.21.1", {"start": v(15, -25.84) * mm, "end": v(14.94, -25.88) * mm});
            skArc(sketch, "E19.21.2", {"start": v(15.97, -25.96) * mm, "mid": v(17.18, -27) * mm, "end": v(18.52, -27.86) * mm});
            skArc(sketch, "E19.21.3", {"start": v(18.52, -27.86) * mm, "mid": v(18.94, -27.95) * mm, "end": v(19.35, -27.82) * mm});
            skLineSegment(sketch, "E19.21.4", {"start": v(19.35, -27.82) * mm, "end": v(19.44, -27.76) * mm});
            skLineSegment(sketch, "E19.21.5", {"start": v(19.52, -27.7) * mm, "end": v(19.44, -27.76) * mm});
            skArc(sketch, "E19.21.6", {"start": v(19.84, -26.93) * mm, "mid": v(19.79, -27.36) * mm, "end": v(19.52, -27.7) * mm});
            skArc(sketch, "E19.21.7", {"start": v(18.94, -23.88) * mm, "mid": v(19.5, -25.37) * mm, "end": v(19.84, -26.93) * mm});
            skArc(sketch, "E19.21.8", {"start": v(18.94, -23.88) * mm, "mid": v(18.88, -23.37) * mm, "end": v(19.16, -22.93) * mm});
            skLineSegment(sketch, "E19.21.9", {"start": v(19.16, -22.93) * mm, "end": v(19.2, -22.89) * mm});
            skArc(sketch, "E19.22.0", {"start": v(20.23, -22.8) * mm, "mid": v(19.74, -22.65) * mm, "end": v(19.26, -22.85) * mm});
            skLineSegment(sketch, "E19.22.1", {"start": v(19.26, -22.85) * mm, "end": v(19.2, -22.89) * mm});
            skArc(sketch, "E19.22.2", {"start": v(20.23, -22.8) * mm, "mid": v(21.6, -23.6) * mm, "end": v(23.08, -24.22) * mm});
            skArc(sketch, "E19.22.3", {"start": v(23.08, -24.22) * mm, "mid": v(23.5, -24.24) * mm, "end": v(23.88, -24.03) * mm});
            skLineSegment(sketch, "E19.22.4", {"start": v(23.88, -24.03) * mm, "end": v(23.96, -23.96) * mm});
            skLineSegment(sketch, "E19.22.5", {"start": v(24.03, -23.88) * mm, "end": v(23.96, -23.96) * mm});
            skArc(sketch, "E19.22.6", {"start": v(24.22, -23.08) * mm, "mid": v(24.24, -23.5) * mm, "end": v(24.03, -23.88) * mm});
            skArc(sketch, "E19.22.7", {"start": v(22.8, -20.23) * mm, "mid": v(23.6, -21.6) * mm, "end": v(24.22, -23.08) * mm});
            skArc(sketch, "E19.22.8", {"start": v(22.8, -20.23) * mm, "mid": v(22.65, -19.74) * mm, "end": v(22.85, -19.26) * mm});
            skLineSegment(sketch, "E19.22.9", {"start": v(22.85, -19.26) * mm, "end": v(22.89, -19.2) * mm});
            skArc(sketch, "E19.23.0", {"start": v(23.88, -18.94) * mm, "mid": v(23.37, -18.88) * mm, "end": v(22.93, -19.16) * mm});
            skLineSegment(sketch, "E19.23.1", {"start": v(22.93, -19.16) * mm, "end": v(22.89, -19.2) * mm});
            skArc(sketch, "E19.23.2", {"start": v(23.88, -18.94) * mm, "mid": v(25.37, -19.5) * mm, "end": v(26.93, -19.84) * mm});
            skArc(sketch, "E19.23.3", {"start": v(26.93, -19.84) * mm, "mid": v(27.36, -19.79) * mm, "end": v(27.7, -19.52) * mm});
            skLineSegment(sketch, "E19.23.4", {"start": v(27.7, -19.52) * mm, "end": v(27.76, -19.44) * mm});
            skLineSegment(sketch, "E19.23.5", {"start": v(27.82, -19.35) * mm, "end": v(27.76, -19.44) * mm});
            skArc(sketch, "E19.23.6", {"start": v(27.86, -18.52) * mm, "mid": v(27.95, -18.94) * mm, "end": v(27.82, -19.35) * mm});
            skArc(sketch, "E19.23.7", {"start": v(25.96, -15.97) * mm, "mid": v(27, -17.18) * mm, "end": v(27.86, -18.52) * mm});
            skArc(sketch, "E19.23.8", {"start": v(25.96, -15.97) * mm, "mid": v(25.74, -15.5) * mm, "end": v(25.84, -15) * mm});
            skLineSegment(sketch, "E19.23.9", {"start": v(25.84, -15) * mm, "end": v(25.88, -14.94) * mm});
            skArc(sketch, "E19.24.0", {"start": v(26.8, -14.5) * mm, "mid": v(26.3, -14.54) * mm, "end": v(25.9, -14.88) * mm});
            skLineSegment(sketch, "E19.24.1", {"start": v(25.9, -14.88) * mm, "end": v(25.88, -14.94) * mm});
            skArc(sketch, "E19.24.2", {"start": v(26.8, -14.5) * mm, "mid": v(28.37, -14.8) * mm, "end": v(29.97, -14.86) * mm});
            skArc(sketch, "E19.24.3", {"start": v(29.97, -14.86) * mm, "mid": v(30.38, -14.74) * mm, "end": v(30.66, -14.41) * mm});
            skLineSegment(sketch, "E19.24.4", {"start": v(30.66, -14.41) * mm, "end": v(30.71, -14.32) * mm});
            skLineSegment(sketch, "E19.24.5", {"start": v(30.75, -14.22) * mm, "end": v(30.71, -14.32) * mm});
            skArc(sketch, "E19.24.6", {"start": v(30.65, -13.4) * mm, "mid": v(30.82, -13.8) * mm, "end": v(30.75, -14.22) * mm});
            skArc(sketch, "E19.24.7", {"start": v(28.34, -11.22) * mm, "mid": v(29.57, -12.23) * mm, "end": v(30.65, -13.4) * mm});
            skArc(sketch, "E19.24.8", {"start": v(28.34, -11.22) * mm, "mid": v(28.04, -10.8) * mm, "end": v(28.05, -10.28) * mm});
            skLineSegment(sketch, "E19.24.9", {"start": v(28.05, -10.28) * mm, "end": v(28.08, -10.22) * mm});
            skArc(sketch, "E19.25.0", {"start": v(28.92, -9.63) * mm, "mid": v(28.42, -9.75) * mm, "end": v(28.1, -10.16) * mm});
            skLineSegment(sketch, "E19.25.1", {"start": v(28.1, -10.16) * mm, "end": v(28.08, -10.22) * mm});
            skArc(sketch, "E19.25.2", {"start": v(28.92, -9.63) * mm, "mid": v(30.51, -9.64) * mm, "end": v(32.1, -9.43) * mm});
            skArc(sketch, "E19.25.3", {"start": v(32.1, -9.43) * mm, "mid": v(32.48, -9.24) * mm, "end": v(32.7, -8.87) * mm});
            skLineSegment(sketch, "E19.25.4", {"start": v(32.7, -8.87) * mm, "end": v(32.73, -8.77) * mm});
            skLineSegment(sketch, "E19.25.5", {"start": v(32.76, -8.67) * mm, "end": v(32.73, -8.77) * mm});
            skArc(sketch, "E19.25.6", {"start": v(32.5, -7.88) * mm, "mid": v(32.74, -8.24) * mm, "end": v(32.76, -8.67) * mm});
            skArc(sketch, "E19.25.7", {"start": v(29.86, -6.12) * mm, "mid": v(31.25, -6.9) * mm, "end": v(32.5, -7.88) * mm});
            skArc(sketch, "E19.25.8", {"start": v(29.86, -6.12) * mm, "mid": v(29.49, -5.76) * mm, "end": v(29.41, -5.25) * mm});
            skLineSegment(sketch, "E19.25.9", {"start": v(29.41, -5.25) * mm, "end": v(29.43, -5.19) * mm});
            skArc(sketch, "E19.26.0", {"start": v(30.15, -4.46) * mm, "mid": v(29.68, -4.67) * mm, "end": v(29.44, -5.12) * mm});
            skLineSegment(sketch, "E19.26.1", {"start": v(29.44, -5.12) * mm, "end": v(29.43, -5.19) * mm});
            skArc(sketch, "E19.26.2", {"start": v(30.15, -4.46) * mm, "mid": v(31.72, -4.2) * mm, "end": v(33.24, -3.72) * mm});
            skArc(sketch, "E19.26.3", {"start": v(33.24, -3.72) * mm, "mid": v(33.59, -3.46) * mm, "end": v(33.75, -3.06) * mm});
            skLineSegment(sketch, "E19.26.4", {"start": v(33.75, -3.06) * mm, "end": v(33.76, -2.95) * mm});
            skLineSegment(sketch, "E19.26.5", {"start": v(33.76, -2.85) * mm, "end": v(33.76, -2.95) * mm});
            skArc(sketch, "E19.26.6", {"start": v(33.38, -2.11) * mm, "mid": v(33.68, -2.43) * mm, "end": v(33.76, -2.85) * mm});
            skArc(sketch, "E19.26.7", {"start": v(30.47, -0.85) * mm, "mid": v(31.97, -1.38) * mm, "end": v(33.38, -2.11) * mm});
            skArc(sketch, "E19.26.8", {"start": v(30.47, -0.85) * mm, "mid": v(30.04, -0.56) * mm, "end": v(29.88, -0.07) * mm});
            skLineSegment(sketch, "E19.26.9", {"start": v(29.88, -0.07) * mm, "end": v(29.88, 0) * mm});
            skArc(sketch, "E19.27.0", {"start": v(30.47, 0.85) * mm, "mid": v(30.04, 0.56) * mm, "end": v(29.88, 0.07) * mm});
            skLineSegment(sketch, "E19.27.1", {"start": v(29.88, 0.07) * mm, "end": v(29.88, 0) * mm});
            skArc(sketch, "E19.27.2", {"start": v(30.47, 0.85) * mm, "mid": v(31.97, 1.38) * mm, "end": v(33.38, 2.11) * mm});
            skArc(sketch, "E19.27.3", {"start": v(33.38, 2.11) * mm, "mid": v(33.68, 2.43) * mm, "end": v(33.76, 2.85) * mm});
            skLineSegment(sketch, "E19.27.4", {"start": v(33.76, 2.85) * mm, "end": v(33.76, 2.95) * mm});
            skLineSegment(sketch, "E19.27.5", {"start": v(33.75, 3.06) * mm, "end": v(33.76, 2.95) * mm});
            skArc(sketch, "E19.27.6", {"start": v(33.24, 3.72) * mm, "mid": v(33.59, 3.46) * mm, "end": v(33.75, 3.06) * mm});
            skArc(sketch, "E19.27.7", {"start": v(30.15, 4.46) * mm, "mid": v(31.72, 4.2) * mm, "end": v(33.24, 3.72) * mm});
            skArc(sketch, "E19.27.8", {"start": v(30.15, 4.46) * mm, "mid": v(29.68, 4.67) * mm, "end": v(29.44, 5.12) * mm});
            skLineSegment(sketch, "E19.27.9", {"start": v(29.44, 5.12) * mm, "end": v(29.43, 5.19) * mm});
            skArc(sketch, "E19.28.0", {"start": v(29.86, 6.12) * mm, "mid": v(29.49, 5.76) * mm, "end": v(29.41, 5.25) * mm});
            skLineSegment(sketch, "E19.28.1", {"start": v(29.41, 5.25) * mm, "end": v(29.43, 5.19) * mm});
            skArc(sketch, "E19.28.2", {"start": v(29.86, 6.12) * mm, "mid": v(31.25, 6.9) * mm, "end": v(32.5, 7.88) * mm});
            skArc(sketch, "E19.28.3", {"start": v(32.5, 7.88) * mm, "mid": v(32.74, 8.24) * mm, "end": v(32.76, 8.67) * mm});
            skLineSegment(sketch, "E19.28.4", {"start": v(32.76, 8.67) * mm, "end": v(32.73, 8.77) * mm});
            skLineSegment(sketch, "E19.28.5", {"start": v(32.7, 8.87) * mm, "end": v(32.73, 8.77) * mm});
            skArc(sketch, "E19.28.6", {"start": v(32.1, 9.43) * mm, "mid": v(32.48, 9.24) * mm, "end": v(32.7, 8.87) * mm});
            skArc(sketch, "E19.28.7", {"start": v(28.92, 9.63) * mm, "mid": v(30.51, 9.64) * mm, "end": v(32.1, 9.43) * mm});
            skArc(sketch, "E19.28.8", {"start": v(28.92, 9.63) * mm, "mid": v(28.42, 9.75) * mm, "end": v(28.1, 10.16) * mm});
            skLineSegment(sketch, "E19.28.9", {"start": v(28.1, 10.16) * mm, "end": v(28.08, 10.22) * mm});
            skArc(sketch, "E19.29.0", {"start": v(28.34, 11.22) * mm, "mid": v(28.04, 10.8) * mm, "end": v(28.05, 10.28) * mm});
            skLineSegment(sketch, "E19.29.1", {"start": v(28.05, 10.28) * mm, "end": v(28.08, 10.22) * mm});
            skArc(sketch, "E19.29.2", {"start": v(28.34, 11.22) * mm, "mid": v(29.57, 12.23) * mm, "end": v(30.65, 13.4) * mm});
            skArc(sketch, "E19.29.3", {"start": v(30.65, 13.4) * mm, "mid": v(30.82, 13.8) * mm, "end": v(30.75, 14.22) * mm});
            skLineSegment(sketch, "E19.29.4", {"start": v(30.75, 14.22) * mm, "end": v(30.71, 14.32) * mm});
            skLineSegment(sketch, "E19.29.5", {"start": v(30.66, 14.41) * mm, "end": v(30.71, 14.32) * mm});
            skArc(sketch, "E19.29.6", {"start": v(29.97, 14.86) * mm, "mid": v(30.38, 14.74) * mm, "end": v(30.66, 14.41) * mm});
            skArc(sketch, "E19.29.7", {"start": v(26.8, 14.5) * mm, "mid": v(28.37, 14.8) * mm, "end": v(29.97, 14.86) * mm});
            skArc(sketch, "E19.29.8", {"start": v(26.8, 14.5) * mm, "mid": v(26.3, 14.54) * mm, "end": v(25.9, 14.88) * mm});
            skLineSegment(sketch, "E19.29.9", {"start": v(25.9, 14.88) * mm, "end": v(25.88, 14.94) * mm});
            skArc(sketch, "E19.30.0", {"start": v(25.96, 15.97) * mm, "mid": v(25.74, 15.5) * mm, "end": v(25.84, 15) * mm});
            skLineSegment(sketch, "E19.30.1", {"start": v(25.84, 15) * mm, "end": v(25.88, 14.94) * mm});
            skArc(sketch, "E19.30.2", {"start": v(25.96, 15.97) * mm, "mid": v(27, 17.18) * mm, "end": v(27.86, 18.52) * mm});
            skArc(sketch, "E19.30.3", {"start": v(27.86, 18.52) * mm, "mid": v(27.95, 18.94) * mm, "end": v(27.82, 19.35) * mm});
            skLineSegment(sketch, "E19.30.4", {"start": v(27.82, 19.35) * mm, "end": v(27.76, 19.44) * mm});
            skLineSegment(sketch, "E19.30.5", {"start": v(27.7, 19.52) * mm, "end": v(27.76, 19.44) * mm});
            skArc(sketch, "E19.30.6", {"start": v(26.93, 19.84) * mm, "mid": v(27.36, 19.79) * mm, "end": v(27.7, 19.52) * mm});
            skArc(sketch, "E19.30.7", {"start": v(23.88, 18.94) * mm, "mid": v(25.37, 19.5) * mm, "end": v(26.93, 19.84) * mm});
            skArc(sketch, "E19.30.8", {"start": v(23.88, 18.94) * mm, "mid": v(23.37, 18.88) * mm, "end": v(22.93, 19.16) * mm});
            skLineSegment(sketch, "E19.30.9", {"start": v(22.93, 19.16) * mm, "end": v(22.89, 19.2) * mm});
            skArc(sketch, "E19.31.0", {"start": v(22.8, 20.23) * mm, "mid": v(22.65, 19.74) * mm, "end": v(22.85, 19.26) * mm});
            skLineSegment(sketch, "E19.31.1", {"start": v(22.85, 19.26) * mm, "end": v(22.89, 19.2) * mm});
            skArc(sketch, "E19.31.2", {"start": v(22.8, 20.23) * mm, "mid": v(23.6, 21.6) * mm, "end": v(24.22, 23.08) * mm});
            skArc(sketch, "E19.31.3", {"start": v(24.22, 23.08) * mm, "mid": v(24.24, 23.5) * mm, "end": v(24.03, 23.88) * mm});
            skLineSegment(sketch, "E19.31.4", {"start": v(24.03, 23.88) * mm, "end": v(23.96, 23.96) * mm});
            skLineSegment(sketch, "E19.31.5", {"start": v(23.88, 24.03) * mm, "end": v(23.96, 23.96) * mm});
            skArc(sketch, "E19.31.6", {"start": v(23.08, 24.22) * mm, "mid": v(23.5, 24.24) * mm, "end": v(23.88, 24.03) * mm});
            skArc(sketch, "E19.31.7", {"start": v(20.23, 22.8) * mm, "mid": v(21.6, 23.6) * mm, "end": v(23.08, 24.22) * mm});
            skArc(sketch, "E19.31.8", {"start": v(20.23, 22.8) * mm, "mid": v(19.74, 22.65) * mm, "end": v(19.26, 22.85) * mm});
            skLineSegment(sketch, "E19.31.9", {"start": v(19.26, 22.85) * mm, "end": v(19.2, 22.89) * mm});
            skArc(sketch, "E19.32.0", {"start": v(18.94, 23.88) * mm, "mid": v(18.88, 23.37) * mm, "end": v(19.16, 22.93) * mm});
            skLineSegment(sketch, "E19.32.1", {"start": v(19.16, 22.93) * mm, "end": v(19.2, 22.89) * mm});
            skArc(sketch, "E19.32.2", {"start": v(18.94, 23.88) * mm, "mid": v(19.5, 25.37) * mm, "end": v(19.84, 26.93) * mm});
            skArc(sketch, "E19.32.3", {"start": v(19.84, 26.93) * mm, "mid": v(19.79, 27.36) * mm, "end": v(19.52, 27.7) * mm});
            skLineSegment(sketch, "E19.32.4", {"start": v(19.52, 27.7) * mm, "end": v(19.44, 27.76) * mm});
            skLineSegment(sketch, "E19.32.5", {"start": v(19.35, 27.82) * mm, "end": v(19.44, 27.76) * mm});
            skArc(sketch, "E19.32.6", {"start": v(18.52, 27.86) * mm, "mid": v(18.94, 27.95) * mm, "end": v(19.35, 27.82) * mm});
            skArc(sketch, "E19.32.7", {"start": v(15.97, 25.96) * mm, "mid": v(17.18, 27) * mm, "end": v(18.52, 27.86) * mm});
            skArc(sketch, "E19.32.8", {"start": v(15.97, 25.96) * mm, "mid": v(15.5, 25.74) * mm, "end": v(15, 25.84) * mm});
            skLineSegment(sketch, "E19.32.9", {"start": v(15, 25.84) * mm, "end": v(14.94, 25.88) * mm});
            skArc(sketch, "E19.33.0", {"start": v(14.5, 26.8) * mm, "mid": v(14.54, 26.3) * mm, "end": v(14.88, 25.9) * mm});
            skLineSegment(sketch, "E19.33.1", {"start": v(14.88, 25.9) * mm, "end": v(14.94, 25.88) * mm});
            skArc(sketch, "E19.33.2", {"start": v(14.5, 26.8) * mm, "mid": v(14.8, 28.37) * mm, "end": v(14.86, 29.97) * mm});
            skArc(sketch, "E19.33.3", {"start": v(14.86, 29.97) * mm, "mid": v(14.74, 30.38) * mm, "end": v(14.41, 30.66) * mm});
            skLineSegment(sketch, "E19.33.4", {"start": v(14.41, 30.66) * mm, "end": v(14.32, 30.71) * mm});
            skLineSegment(sketch, "E19.33.5", {"start": v(14.22, 30.75) * mm, "end": v(14.32, 30.71) * mm});
            skArc(sketch, "E19.33.6", {"start": v(13.4, 30.65) * mm, "mid": v(13.8, 30.82) * mm, "end": v(14.22, 30.75) * mm});
            skArc(sketch, "E19.33.7", {"start": v(11.22, 28.34) * mm, "mid": v(12.23, 29.57) * mm, "end": v(13.4, 30.65) * mm});
            skArc(sketch, "E19.33.8", {"start": v(11.22, 28.34) * mm, "mid": v(10.8, 28.04) * mm, "end": v(10.28, 28.05) * mm});
            skLineSegment(sketch, "E19.33.9", {"start": v(10.28, 28.05) * mm, "end": v(10.22, 28.08) * mm});
            skArc(sketch, "E19.34.0", {"start": v(9.63, 28.92) * mm, "mid": v(9.75, 28.42) * mm, "end": v(10.16, 28.1) * mm});
            skLineSegment(sketch, "E19.34.1", {"start": v(10.16, 28.1) * mm, "end": v(10.22, 28.08) * mm});
            skArc(sketch, "E19.34.2", {"start": v(9.63, 28.92) * mm, "mid": v(9.64, 30.51) * mm, "end": v(9.43, 32.1) * mm});
            skArc(sketch, "E19.34.3", {"start": v(9.43, 32.1) * mm, "mid": v(9.24, 32.48) * mm, "end": v(8.87, 32.7) * mm});
            skLineSegment(sketch, "E19.34.4", {"start": v(8.87, 32.7) * mm, "end": v(8.77, 32.73) * mm});
            skLineSegment(sketch, "E19.34.5", {"start": v(8.67, 32.76) * mm, "end": v(8.77, 32.73) * mm});
            skArc(sketch, "E19.34.6", {"start": v(7.88, 32.51) * mm, "mid": v(8.24, 32.74) * mm, "end": v(8.67, 32.76) * mm});
            skArc(sketch, "E19.34.7", {"start": v(6.12, 29.86) * mm, "mid": v(6.9, 31.25) * mm, "end": v(7.88, 32.51) * mm});
            skArc(sketch, "E19.34.8", {"start": v(6.12, 29.86) * mm, "mid": v(5.76, 29.49) * mm, "end": v(5.25, 29.41) * mm});
            skLineSegment(sketch, "E19.34.9", {"start": v(5.25, 29.41) * mm, "end": v(5.19, 29.43) * mm});
            skArc(sketch, "E19.35.0", {"start": v(4.46, 30.15) * mm, "mid": v(4.67, 29.68) * mm, "end": v(5.12, 29.44) * mm});
            skLineSegment(sketch, "E19.35.1", {"start": v(5.12, 29.44) * mm, "end": v(5.19, 29.43) * mm});
            skArc(sketch, "E19.35.2", {"start": v(4.46, 30.15) * mm, "mid": v(4.2, 31.72) * mm, "end": v(3.72, 33.24) * mm});
            skArc(sketch, "E19.35.3", {"start": v(3.72, 33.24) * mm, "mid": v(3.46, 33.59) * mm, "end": v(3.06, 33.75) * mm});
            skLineSegment(sketch, "E19.35.4", {"start": v(3.06, 33.75) * mm, "end": v(2.95, 33.76) * mm});
            skLineSegment(sketch, "E19.35.5", {"start": v(2.85, 33.76) * mm, "end": v(2.95, 33.76) * mm});
            skArc(sketch, "E19.35.6", {"start": v(2.11, 33.38) * mm, "mid": v(2.43, 33.68) * mm, "end": v(2.85, 33.76) * mm});
            skArc(sketch, "E19.35.7", {"start": v(0.85, 30.47) * mm, "mid": v(1.38, 31.97) * mm, "end": v(2.11, 33.38) * mm});
            skArc(sketch, "E19.35.8", {"start": v(0.85, 30.47) * mm, "mid": v(0.56, 30.04) * mm, "end": v(0.07, 29.88) * mm});
            skLineSegment(sketch, "E19.35.9", {"start": v(0.07, 29.88) * mm, "end": v(0, 29.88) * mm});
            skLineSegment(sketch, "E20", {"start": v(0, 0) * mm, "end": v(-5.13, -5.13) * mm, "construction": true});
            skCircle(sketch, "E21", {"center": v(0, 0) * mm, "radius": 1 * mm});
            skCircle(sketch, "E22.cCircle", {"center": v(0, 0) * mm, "radius": 4.13 * mm, "construction": true});
            skLineSegment(sketch, "E22.0", {"start": v(4.85, 1.58) * mm, "end": v(3, -4.13) * mm});
            skLineSegment(sketch, "E22.1", {"start": v(3, -4.13) * mm, "end": v(-3, -4.13) * mm});
            skLineSegment(sketch, "E22.2", {"start": v(-3, -4.13) * mm, "end": v(-4.85, 1.58) * mm});
            skLineSegment(sketch, "E22.3", {"start": v(-4.85, 1.58) * mm, "end": v(0, 5.1) * mm});
            skLineSegment(sketch, "E22.4", {"start": v(0, 5.1) * mm, "end": v(4.85, 1.58) * mm});
            skPoint(sketch, "E22.0.midPoint", {"position": v(3.92, -1.27) * mm});
            skSolve(sketch);
        }
        {
            var Q0;
            Q0=makeQuery(id+"F0.imprint","IMPRINT",FACE,{"disambiguationData":[TD([[makeQuery(id+"F0.imprint","IMPRINT",EDGE,{"derivedFrom":sQuery(id+"F0.wireOp",EDGE,"E9.trimOffspring")}),1.0]])]});
            extrude(context, id + "F1", {"entities" : qUnion([Q0]), "endBound" : BoundingType.SYMMETRIC, "depth" : 10 * mm});
        }
    });
